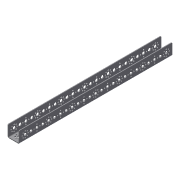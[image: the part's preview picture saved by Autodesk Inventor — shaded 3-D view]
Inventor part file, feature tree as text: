
AUTODESK INVENTOR PART (.ipt)
format: ipt  version: 2013 (Build 170138000, 138)  size: 547,328 bytes
history: native  units: in
note: dims shown in document units (in); Inventor stores cm internally (conversion verified against a paired STEP export)
features: hole x28, other x5, sketch x3
ambient origin geometry x8: Origin, YZ Plane, XZ Plane, XY Plane, X Axis, Y Axis, Z Axis, Center Point
bodies: Solid1 (feature_tree)
feature tree (36):
  other  "Tetrix Channel 416mm.ipt"
  other  "Blocks"
  hole  "Hole Pattern 4"  [1 undecoded]
  hole  "Hole Pattern 8"  [1 undecoded]
  other  "416 mm hole pattern"
  other  "Solid1::Tetrix Channel 416mm.ipt"
  other  "TaggingFeature1"
  sketch  "Sketch1"  dims[d0=0.3937in]
  sketch  "Sketch2"  dims[d1=16.378in d3=0.6299in d4=0.1457in d6=0.6299in d8=0.6299in d9=0.6299in d10=0.315in d13=0.1457in d14=0.315in d15=3.1496in d20=0.6299in d21=0.6299in d22=0.6299in d23=0.6299in d25=0.6299in d26=0.6299in d27=0.0787in d28=0.0787in d29=0.0394in d30=0.1575in d31=0.0787in d32=1.2598in d33=90.0deg d34=0.0787in d35=0.315in d36=0.0787in d37=0.0787in d38=0.6299in d39=0.6299in d40=0.6299in d41=0.6299in d42=0.6299in d43=0.6299in d45=0.6299in d47=0.0in d48=0.0787in d17=360.0deg]
  sketch  "Sketch3"
  hole  "Hole Pattern 4:1"  [1 undecoded]
  hole  "Hole Pattern 8:1"  [1 undecoded]
  hole  "Hole Pattern 8:2"  [1 undecoded]
  hole  "Hole Pattern 4:2"  [1 undecoded]
  hole  "Hole Pattern 8:3"  [1 undecoded]
  hole  "Hole Pattern 4:3"  [1 undecoded]
  hole  "Hole Pattern 8:4"  [1 undecoded]
  hole  "Hole Pattern 4:4"  [1 undecoded]
  hole  "Hole Pattern 8:5"  [1 undecoded]
  hole  "Hole Pattern 8:6"  [1 undecoded]
  hole  "Hole Pattern 4:5"  [1 undecoded]
  hole  "Hole Pattern 8:7"  [1 undecoded]
  hole  "Hole Pattern 4:6"  [1 undecoded]
  hole  "Hole Pattern 4:1_1"  [1 undecoded]
  hole  "Hole Pattern 8:1_1"  [1 undecoded]
  hole  "Hole Pattern 8:2_1"  [1 undecoded]
  hole  "Hole Pattern 4:2_1"  [1 undecoded]
  hole  "Hole Pattern 8:3_1"  [1 undecoded]
  hole  "Hole Pattern 4:3_1"  [1 undecoded]
  hole  "Hole Pattern 8:4_1"  [1 undecoded]
  hole  "Hole Pattern 4:4_1"  [1 undecoded]
  hole  "Hole Pattern 8:5_1"  [1 undecoded]
  hole  "Hole Pattern 8:6_1"  [1 undecoded]
  hole  "Hole Pattern 4:5_1"  [1 undecoded]
  hole  "Hole Pattern 8:7_1"  [1 undecoded]
  hole  "Hole Pattern 4:6_1"  [1 undecoded]
note: 28 required parameter values undecoded (feature->parameter linkage not recoverable at this tier; creation-order binding heuristic only, values carry confidence <= 0.55)
